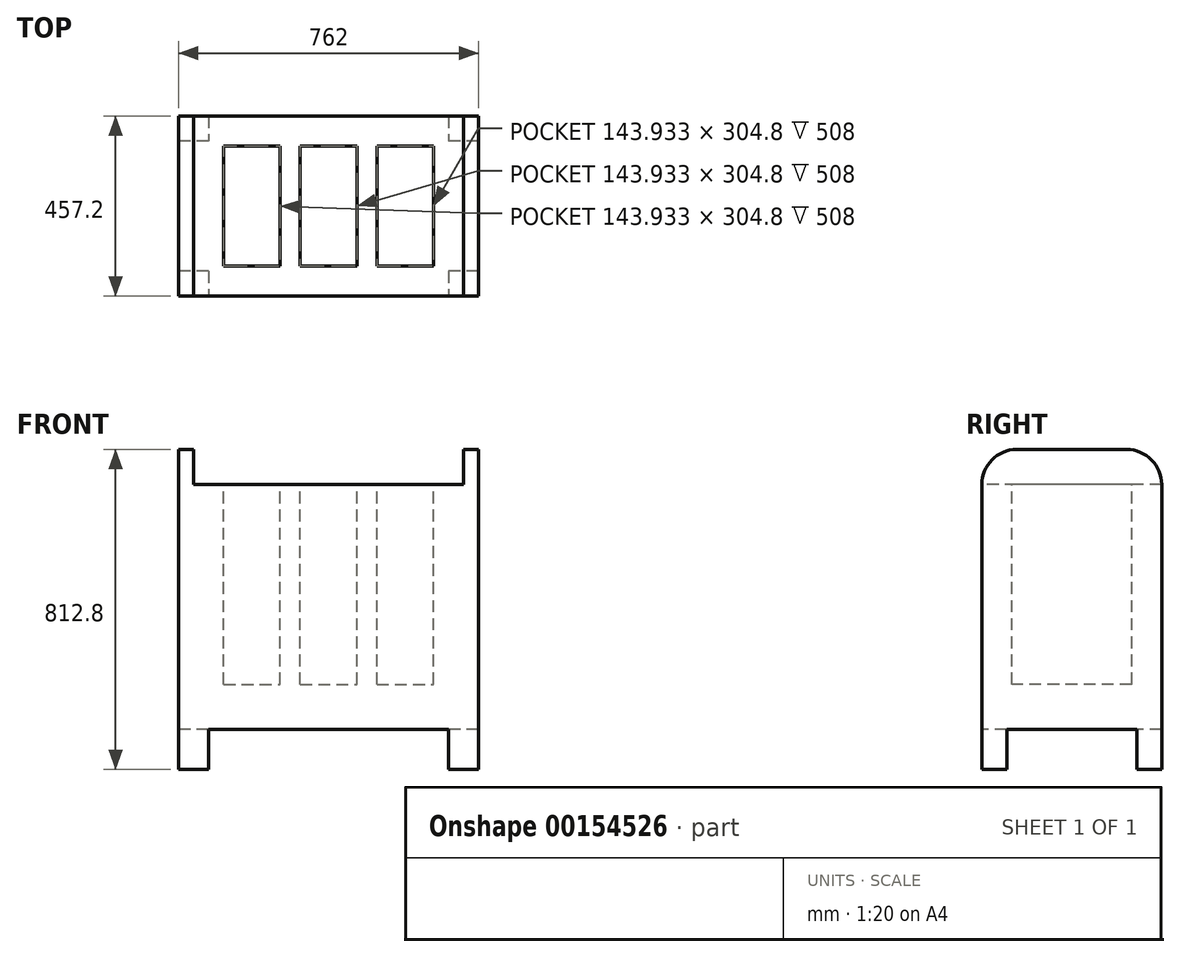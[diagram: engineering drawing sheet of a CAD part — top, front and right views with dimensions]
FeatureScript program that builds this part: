
annotation { "Feature Type Name" : "Feature", "Feature Type Description" : "" }
export const myFeature = defineFeature(function(context is Context, id is Id, definition is map)
    precondition{}
    {
        {
            var Q0;
            Q0=qCreatedBy(makeId("Right.planeOp"),FACE);
            var sketch = newSketch(context, id + "F0", { "sketchPlane" : qUnion([Q0])});
            skLineSegment(sketch, "E0.bottom", {"start": v(0, 0) * mm, "end": v(457.2, 0) * mm});
            skLineSegment(sketch, "E0.top", {"start": v(88.9, 812.8) * mm, "end": v(368.3, 812.8) * mm});
            skLineSegment(sketch, "E0.left", {"start": v(0, 0) * mm, "end": v(0, 723.9) * mm});
            skLineSegment(sketch, "E0.right", {"start": v(457.2, 0) * mm, "end": v(457.2, 723.9) * mm});
            skPoint(sketch, "E1.visualSharp", {"position": v(0, 812.8) * mm});
            skArc(sketch, "E1.filletArc", {"start": v(88.9, 812.8) * mm, "mid": v(26.04, 786.76) * mm, "end": v(0, 723.9) * mm});
            skPoint(sketch, "E2.visualSharp", {"position": v(457.2, 812.8) * mm});
            skArc(sketch, "E2.filletArc", {"start": v(457.2, 723.9) * mm, "mid": v(431.16, 786.76) * mm, "end": v(368.3, 812.8) * mm});
            skLineSegment(sketch, "E3", {"start": v(457.2, 723.9) * mm, "end": v(0, 723.9) * mm});
            skLineSegment(sketch, "E4.bottom", {"start": v(63.5, 0) * mm, "end": v(393.7, 0) * mm});
            skLineSegment(sketch, "E4.top", {"start": v(63.5, 101.6) * mm, "end": v(393.7, 101.6) * mm});
            skLineSegment(sketch, "E4.left", {"start": v(63.5, 0) * mm, "end": v(63.5, 101.6) * mm});
            skLineSegment(sketch, "E4.right", {"start": v(393.7, 0) * mm, "end": v(393.7, 101.6) * mm});
            skSolve(sketch);
        }
        {
            var Q0;
            Q0=makeQuery(id+"F0.imprint","IMPRINT",FACE,{"disambiguationData":[TD([[makeQuery(id+"F0.imprint","IMPRINT",EDGE,{"derivedFrom":sQuery(id+"F0.wireOp",EDGE,"E0.top")}),-1.0]])]});
            var Q1;
            {var subQ1=sQuery(id+"F0.wireOp",EDGE,"E0.left");Q1=makeQuery(id+"F0.imprint","IMPRINT",FACE,{"disambiguationData":[TD([[makeQuery(id+"F0.imprint","IMPRINT",EDGE,{"derivedFrom":subQ1}),-1.0]])]});}
            extrude(context, id + "F1", {"entities" : qUnion([Q0, Q1]), "depth" : 762 * mm});
        }
        {
            var Q0;
            Q0=makeQuery(id+"F1.opExtrude","SWEPT_FACE",FACE,{"disambiguationData":[OSD([sQuery(id+"F0.wireOp",EDGE,"E0.left")])]});
            var sketch = newSketch(context, id + "F2", { "sketchPlane" : qUnion([Q0])});
            skLineSegment(sketch, "E5.bottom", {"start": v(685.8, 0) * mm, "end": v(76.2, 0) * mm});
            skLineSegment(sketch, "E5.top", {"start": v(685.8, 101.6) * mm, "end": v(76.2, 101.6) * mm});
            skLineSegment(sketch, "E5.left", {"start": v(685.8, 0) * mm, "end": v(685.8, 101.6) * mm});
            skLineSegment(sketch, "E5.right", {"start": v(76.2, 0) * mm, "end": v(76.2, 101.6) * mm});
            skLineSegment(sketch, "E6.bottom", {"start": v(38.1, 723.9) * mm, "end": v(723.9, 723.9) * mm});
            skLineSegment(sketch, "E6.top", {"start": v(38.1, 812.8) * mm, "end": v(723.9, 812.8) * mm});
            skLineSegment(sketch, "E6.left", {"start": v(38.1, 723.9) * mm, "end": v(38.1, 812.8) * mm});
            skLineSegment(sketch, "E6.right", {"start": v(723.9, 723.9) * mm, "end": v(723.9, 812.8) * mm});
            skSolve(sketch);
        }
        {
            var Q0;
            Q0=makeQuery(id+"F2.imprint","IMPRINT",FACE,{"disambiguationData":[TD([[makeQuery(id+"F2.imprint","IMPRINT",EDGE,{"derivedFrom":sQuery(id+"F2.wireOp",EDGE,"E6.bottom")}),-1.0]])]});
            var Q1;
            Q1=makeQuery(id+"F2.imprint","IMPRINT",FACE,{"disambiguationData":[TD([[makeQuery(id+"F2.imprint","IMPRINT",EDGE,{"derivedFrom":sQuery(id+"F2.wireOp",EDGE,"E5.bottom")}),-1.0]])]});
            extrude(context, id + "F3", {"entities" : qUnion([Q0, Q1]), "operationType" : NewBodyOperationType.REMOVE, "endBound" : BoundingType.THROUGH_ALL, "oppositeDirection" : true, "depth" : 30.48 * mm});
        }
        {
            var Q0;
            Q0=makeQuery(id+"F3.boolean.opBoolean","COPY",FACE,{"derivedFrom":makeQuery(id+"F3.opExtrude","SWEPT_FACE",FACE,{"disambiguationData":[OSD([sQuery(id+"F2.wireOp",EDGE,"E6.bottom")])]})});
            var sketch = newSketch(context, id + "F4", { "sketchPlane" : qUnion([Q0])});
            skLineSegment(sketch, "E7.bottom", {"start": v(309.03, 381) * mm, "end": v(452.97, 381) * mm});
            skLineSegment(sketch, "E7.top", {"start": v(309.03, 76.2) * mm, "end": v(452.97, 76.2) * mm});
            skLineSegment(sketch, "E7.left", {"start": v(452.97, 381) * mm, "end": v(452.97, 76.2) * mm});
            skLineSegment(sketch, "E7.right", {"start": v(309.03, 381) * mm, "end": v(309.03, 76.2) * mm});
            skLineSegment(sketch, "E8.bottom", {"start": v(503.77, 381) * mm, "end": v(647.7, 381) * mm});
            skLineSegment(sketch, "E8.top", {"start": v(503.77, 76.2) * mm, "end": v(647.7, 76.2) * mm});
            skLineSegment(sketch, "E8.left", {"start": v(503.77, 381) * mm, "end": v(503.77, 76.2) * mm});
            skLineSegment(sketch, "E8.right", {"start": v(647.7, 381) * mm, "end": v(647.7, 76.2) * mm});
            skLineSegment(sketch, "E9.bottom", {"start": v(114.3, 381) * mm, "end": v(258.23, 381) * mm});
            skLineSegment(sketch, "E9.top", {"start": v(114.3, 76.2) * mm, "end": v(258.23, 76.2) * mm});
            skLineSegment(sketch, "E9.left", {"start": v(114.3, 381) * mm, "end": v(114.3, 76.2) * mm});
            skLineSegment(sketch, "E9.right", {"start": v(258.23, 381) * mm, "end": v(258.23, 76.2) * mm});
            skSolve(sketch);
        }
        {
            var Q0;
            Q0=makeQuery(id+"F4.imprint","IMPRINT",FACE,{"disambiguationData":[TD([[makeQuery(id+"F4.imprint","IMPRINT",EDGE,{"derivedFrom":sQuery(id+"F4.wireOp",EDGE,"E9.bottom")}),-1.0]])]});
            var Q1;
            Q1=makeQuery(id+"F4.imprint","IMPRINT",FACE,{"disambiguationData":[TD([[makeQuery(id+"F4.imprint","IMPRINT",EDGE,{"derivedFrom":sQuery(id+"F4.wireOp",EDGE,"E7.bottom")}),-1.0]])]});
            var Q2;
            Q2=makeQuery(id+"F4.imprint","IMPRINT",FACE,{"disambiguationData":[TD([[makeQuery(id+"F4.imprint","IMPRINT",EDGE,{"derivedFrom":sQuery(id+"F4.wireOp",EDGE,"E8.bottom")}),-1.0]])]});
            extrude(context, id + "F5", {"entities" : qUnion([Q0, Q1, Q2]), "operationType" : NewBodyOperationType.REMOVE, "oppositeDirection" : true, "depth" : 508 * mm});
        }
    });
